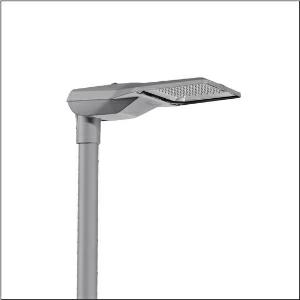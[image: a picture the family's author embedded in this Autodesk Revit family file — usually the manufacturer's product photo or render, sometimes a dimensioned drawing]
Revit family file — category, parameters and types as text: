
# Revit family: streetlight_sl_21_midi___pl52_5xe3h43s08lb_5466
name_source: partatom
category: Lighting Fixtures
units: mm (PartAtom-declared; Revit-internal decimal feet)

## family parameters
Cut with Voids When Loaded = No
Host = Face
Light Source = No
Part Type = Normal
Room Calculation Point = No
Round Connector Dimension = Use Diameter
Shared = No

## types (1)
- --- (1 x LED, 14690 lm, 98.3 W, 4000K)
    Apparent Load = 98 VA
    CIE Flux Codes = 27 59 98 100 100
    Color Rendering = 70
    Color Temperature = 4000K
    Default Elevation = 1800 mm
    Description = Streetlight SL 21 midi, mast luminaire, primary light control with lens, of PMMA, primary optical cover: cover, of toughened safety glass, transparent, light distribution: PL52, light emission: direct distribution, primary light characteristic: asymmetric, installation type: side-entry, post-top, LED, High Power LED, rated luminous flux: 14.690lm, luminous efficacy: 149lm/W, light colour: 740, colour temperature: 4000K, control: overheat protection, constant luminous flux control, time-dependent luminous flux control, flexible luminous flux parameterisation, presetting dimming logarithmic, mains connection: 230..240V, AC, 50/60Hz, start of lifetime: 98W, end of service life: 101W, reduction: 45W, luminaire housing, of diecast aluminium, powder-coated, Siteco® metallic grey (DB 702S), corrosivity category C5 mid according to DIN EN ISO 12944, please order mast flange separately, inclination adjustable: 0°, 5°, 10°, 15°, sealing non-destructively replaceable, multi-level sealing system, length: 644mm, width: 335mm, height: 110mm, mast flange for spigot size: 42mm (side-entry): 5XC10008XM4, 60/48mm (side-entry/post-top): 5XC10108XM2, 76/60mm (side-entry/post-top): 5XC10108XM1, Smart Interface above, protection rating (complete): IP66, insulation class (complete): insulation class II (safety insulation), certification: CE, ENEC, ENEC+, VDE, impact resistance: IK09, permissible operating ambient temperature for outdoor applications: -40..+50°C, standard-compliant lighting for roads and squares, packaging unit: 1 piece

Light Distribution: PL52
    Height = 111 mm
    Lamp = 1 x LED
    Lamp Light Flux = 14690 lm
    Lamp Power = 98.3 W
    Lamp count = 1
    Length = 644 mm
    Luminous efficacy = 149 lm/W
    Manufacturer = Siteco
    ModVariant = No
    Model = 5XE3H43S08LB
    Number of Poles = 1
    OnlyDefault = Yes
    Power Factor = 1
    Product Name = Streetlight SL 21 midi | PL52
    Product group = mast luminaire | pylon top
    ProductGroupID = 6100
    Protection Class = Protection class II
    Protection Degree = IP 66
    RLX_Detail_Level = 1
    RLX_Emergency_Light_Flux = 0 lm
    RLX_Emergency_Type = 0
    RLX_Emergency_Type_DB = No
    RlxData = <blob elided: 100269 chars, md5=e6c370e7>
    Socket = socket
    Standby Power = 0 W
    System Light Flux = 14690 lm
    System Power = 98 W
    Type Comments = factory setting: luminous flux: 100 % | dim-lin: 254 | 1020 mA
    Type Image = l_1004302.jpg
    URL = http://relux.com
    VarID = @adj_143103
    Voltage = 0 V
    Weight = 0.00 kg
    Width = 336 mm

## geometry (parser evidence)
native form markers: Blend x4, Sweep x11
no freeform markers — native parametric forms only
